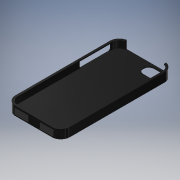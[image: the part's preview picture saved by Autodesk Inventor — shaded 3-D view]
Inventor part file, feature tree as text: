
AUTODESK INVENTOR PART (.ipt)
format: ipt  version: 2019 (Build 230136000, 136)  size: 371,712 bytes
history: native  units: mm
features: sketch x15, extrude x14, other x1, sweep x1, fillet x1
ambient origin geometry x8: Origin, YZ Plane, XZ Plane, XY Plane, X Axis, Y Axis, Z Axis, Center Point
bodies: Body1 (feature_tree)
feature tree (32):
  other  "솔리드1"
  extrude  "돌출1"  Depth=124.3mm
  sketch  "Sketch2"  dims[d0=59.0mm d1=124.3mm]
  sweep  "스윕1"
  extrude  "돌출2"  Depth=8.9mm
  extrude  "돌출3"  TaperAngle=0.0deg  [1 undecoded]
  extrude  "돌출6"  Depth=1.0mm
  extrude  "Extrusion8"  TaperAngle=0.0deg  [1 undecoded]
  fillet  "Fillet8"  Radius=44.0mm
  extrude  "Extrusion9"  Depth=22.0mm
  extrude  "Extrusion10"  Depth=6.0mm
  extrude  "Extrusion11"  Depth=2.0mm
  extrude  "Extrusion12"  Depth=1.0mm TaperAngle=0.0deg
  extrude  "Extrusion13"  Depth=1.0mm
  extrude  "Extrusion14"  TaperAngle=0.0deg  [1 undecoded]
  extrude  "Extrusion15"  Depth=9.9mm
  extrude  "Extrusion16"  TaperAngle=90.0deg  [1 undecoded]
  extrude  "Extrusion17"  Depth=2.3mm
  sketch  "스케치1"
  sketch  "스케치5"
  sketch  "스케치6"
  sketch  "스케치9"
  sketch  "Sketch12"  dims[d2=9.3mm d3=1.0mm d4=0.0mm]
  sketch  "Sketch13"  dims[d5=8.9mm d6=1.3mm]
  sketch  "Sketch14"  dims[d7=1.0mm d9=0.0mm]
  sketch  "Sketch15"  dims[d12=44.0mm d13=1.0mm]
  sketch  "Sketch16"  dims[d14=22.0mm d15=0.0mm d16=0.0mm d17=44.0mm]
  sketch  "Sketch17"  dims[d18=22.0mm d19=62.15mm]
  sketch  "Sketch18"  dims[d20=1.0mm d21=0.0mm d36=6.0mm]
  sketch  "Sketch19"  dims[d37=8.0mm d38=2.0mm]
  sketch  "Sketch20"  dims[d39=11.5mm d40=1.0mm d41=0.0mm]
  sketch  "Sketch21"  dims[d44=0.0mm d45=1.0mm d46=0.0mm d47=9.9mm d48=90.0deg d50=2.3mm d51=35.0mm d52=90.0deg d53=8.9mm d54=90.0deg d55=35.0mm d56=90.0deg d57=8.9mm d58=90.0deg d59=1.5mm d60=180.0deg d61=35.0mm d62=90.0deg d63=7.4mm d64=35.0mm d65=10.0mm d66=0.0mm d67=2.0mm d68=44.0mm d69=1.0mm d70=0.8415mm d71=0.0mm d72=44.0mm d73=1.0mm d74=0.8415mm d75=0.0mm d76=22.0mm d77=180.0deg d78=6.0mm d79=1.0mm d80=6.0mm d81=1.0mm d82=8.9mm d83=0.0mm d84=1.0mm d85=2.347mm d86=44.0mm d87=0.0mm d88=1.0mm d89=1.017mm d90=21.0mm d91=90.0deg d92=0.5mm d93=85.0mm d94=0.5mm d95=85.0mm d96=2.1mm d97=0.0mm d98=1.0mm d99=85.0mm d100=1.1mm d101=2.1mm d102=0.0mm d103=0.0mm d104=24.7mm d105=180.0deg d106=1.0mm d107=85.0mm d108=24.7mm d109=0.0mm d110=1.0mm d111=85.0mm d112=2.1mm d113=0.0mm d114=1.0mm d115=85.0mm d116=1.0mm d117=0.0mm d118=1.0mm d119=85.0mm d120=1.0mm d121=0.0mm]
note: 4 required parameter values undecoded (feature->parameter linkage not recoverable at this tier; creation-order binding heuristic only, values carry confidence <= 0.55)
